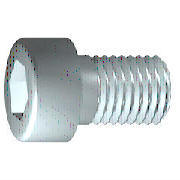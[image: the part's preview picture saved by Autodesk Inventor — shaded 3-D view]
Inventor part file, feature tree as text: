
AUTODESK INVENTOR PART (.ipt)
format: ipt  version: 2015 (Build 190159000, 159)  size: 188,928 bytes
history: native  units: mm (DEFAULTED — no unit token found)
features: sketch x2, other x1, extrude x1, plane x1, fillet x1
ambient origin geometry x7: Origin, YZ Plane, XY Plane, X Axis, Y Axis, Z Axis, Center Point
bodies: Body1 (feature_tree)
feature tree (6):
  other  "Bryła"
  extrude  "Szczelina"  Depth=27.5mm
  plane  "Work Plane1"
  fillet  "Fillet2"  Radius=0.61355mm
  sketch  "Szkic1"
  sketch  "Szkic2"
